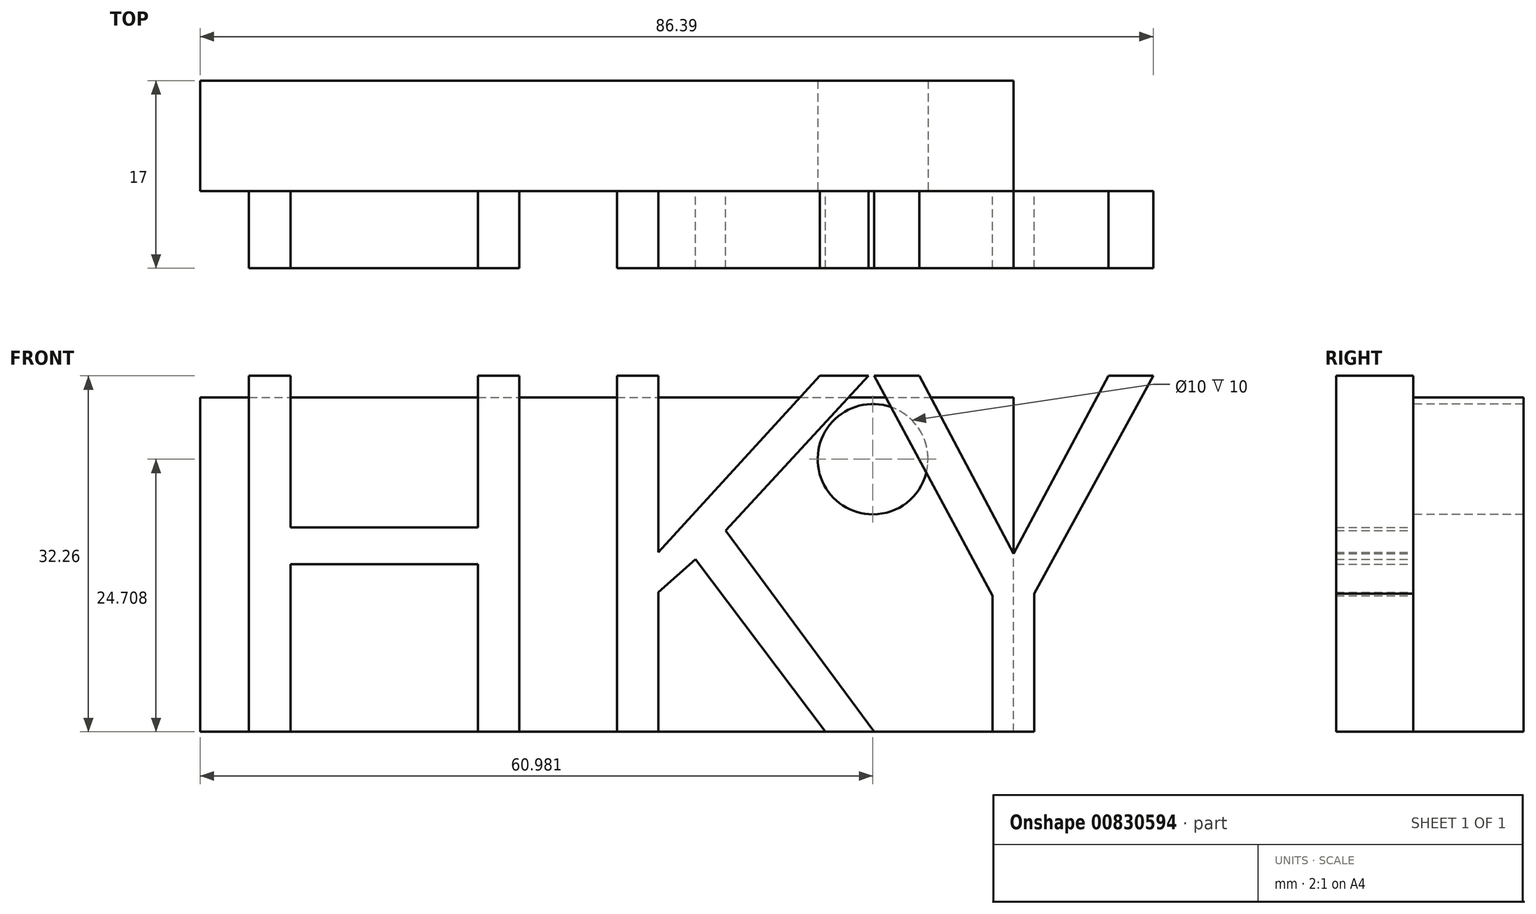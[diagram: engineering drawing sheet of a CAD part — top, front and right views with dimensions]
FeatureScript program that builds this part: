
annotation { "Feature Type Name" : "Feature", "Feature Type Description" : "" }
export const myFeature = defineFeature(function(context is Context, id is Id, definition is map)
    precondition{}
    {
        {
            var Q0;
            Q0=qCreatedBy(makeId("Front.planeOp"),FACE);
            var sketch = newSketch(context, id + "F0", { "sketchPlane" : qUnion([Q0])});
            skLineSegment(sketch, "E0.bottom", {"start": v(0, 0) * mm, "end": v(73.72, 0) * mm});
            skLineSegment(sketch, "E0.top", {"start": v(0, 30.3) * mm, "end": v(73.72, 30.3) * mm});
            skLineSegment(sketch, "E0.left", {"start": v(0, 0) * mm, "end": v(0, 30.3) * mm});
            skLineSegment(sketch, "E0.right", {"start": v(73.72, 0) * mm, "end": v(73.72, 30.3) * mm});
            skSolve(sketch);
        }
        {
            var Q0;
            Q0=makeQuery(id+"F0.imprint","IMPRINT",FACE,{"disambiguationData":[TD([[makeQuery(id+"F0.imprint","IMPRINT",EDGE,{"derivedFrom":sQuery(id+"F0.wireOp",EDGE,"E0.bottom")}),1.0]])]});
            extrude(context, id + "F1", {"entities" : qUnion([Q0]), "depth" : 10 * mm, "offsetDistance" : 25.4 * mm});
        }
        {
            var Q0;
            Q0=makeQuery(id+"F1.opExtrude","CAP_FACE",FACE,{"disambiguationData":[OSD([sQuery(id+"F0.wireOp",EDGE,"E0.bottom"),sQuery(id+"F0.wireOp",EDGE,"E0.top"),sQuery(id+"F0.wireOp",EDGE,"E0.left"),sQuery(id+"F0.wireOp",EDGE,"E0.right")])],"isStart":false});
            var sketch = newSketch(context, id + "F2", { "sketchPlane" : qUnion([Q0])});
            skText(sketch, "E1", { "text": "HKY", "fontName": "OpenSans-Regular.ttf"});
            const initialGuessF2  = {"E1": [0, 0, 1, 0, 0.03254]};
            skSetInitialGuess(sketch, initialGuessF2);
            skSolve(sketch);
        }
        {
            var Q0;
            Q0 = qSketchRegion(id + "F2", true);
            extrude(context, id + "F3", {"entities" : qUnion([Q0]), "operationType" : NewBodyOperationType.ADD, "depth" : 7 * mm, "offsetDistance" : 25.4 * mm});
        }
        {
            var Q0;
            {var subQ0=sQuery(id+"F0.wireOp",EDGE,"E0.top");var subQ1=sQuery(id+"F0.wireOp",EDGE,"E0.right");var subQ2=sQuery(id+"F0.wireOp",EDGE,"E0.bottom");var subQ3=sQuery(id+"F0.wireOp",EDGE,"E0.left");Q0=makeQuery(id+"F3.boolean.opBoolean","SPLIT",FACE,{"disambiguationData":[TD([makeQuery(id+"F1.opExtrude","SWEPT_FACE",FACE,{"disambiguationData":[OSD([subQ0])]})])],"derivedFrom":makeQuery(id+"F1.opExtrude","CAP_FACE",FACE,{"disambiguationData":[OSD([subQ2,subQ0,subQ3,subQ1])],"isStart":false})});}
            var sketch = newSketch(context, id + "F4", { "sketchPlane" : qUnion([Q0])});
            skCircle(sketch, "E2", {"center": v(60.98, 24.7) * mm, "radius": 3.23 * mm});
            skSolve(sketch);
        }
        {
            var Q0;
            Q0=sQuery(id+"F4.wireOp",VERTEX,"E2.center");
            var Q1;
            Q1=makeQuery(id+"F1.opExtrude","SWEPT_BODY",BODY,{"disambiguationData":[OSD([sQuery(id+"F0.wireOp",EDGE,"E0.bottom"),sQuery(id+"F0.wireOp",EDGE,"E0.top"),sQuery(id+"F0.wireOp",EDGE,"E0.left"),sQuery(id+"F0.wireOp",EDGE,"E0.right")])]});
            hole(context, id + "F5", {"style" : HoleStyle.SIMPLE, "endStyle" : HoleEndStyle.THROUGH, "holeDiameter" : 10 * mm, "majorDiameter" : 6.35 * mm, "isTappedThrough" : true, "tappedDepth" : 12.7 * mm, "tapClearance" : 3, "locations" : qUnion([Q0]), "scope" : qUnion([Q1])});
        }
    });
